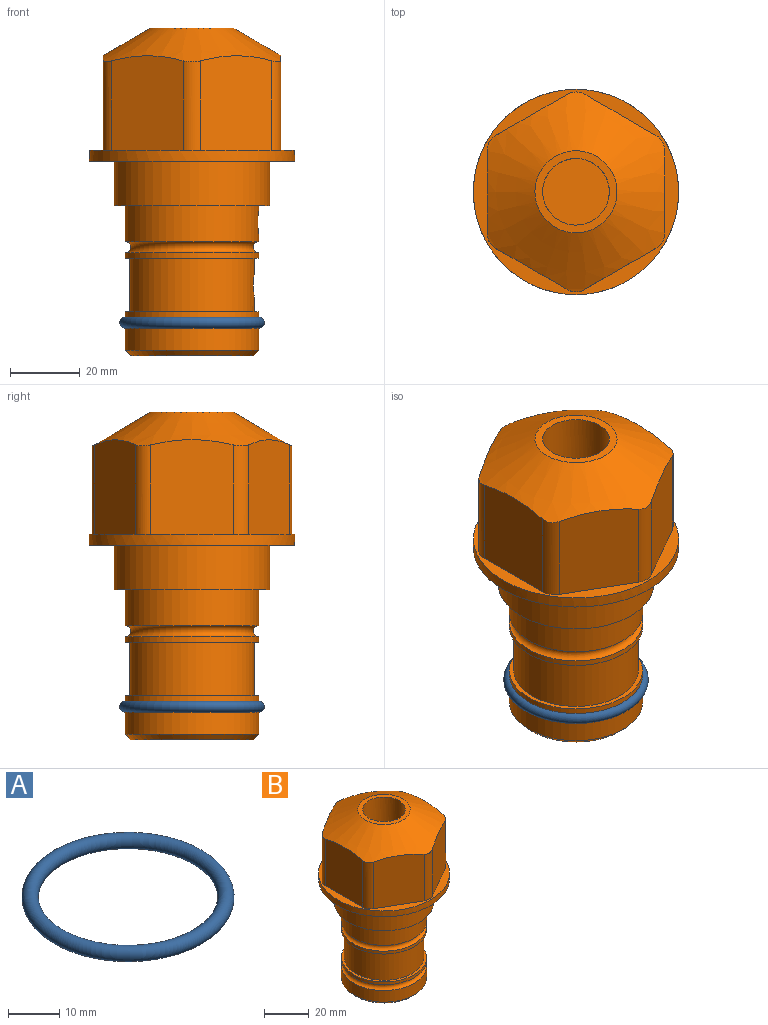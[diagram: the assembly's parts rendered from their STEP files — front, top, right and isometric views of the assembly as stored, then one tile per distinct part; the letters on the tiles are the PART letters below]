
ASSEMBLY  parts=2 mates=1
PART A: 1 faces, bbox 44.7x44.7x3.2 mm
  f0: torus R=19.05mm, axis (0,0,1), area 1193.9mm2
PART B: 36 faces, bbox 58.7x58.7x93.7 mm
  f0: cylinder r=17.78mm len=35.56mm, axis (0,0,1), area 1670.8mm2, adj f23,f24,f31
  f1: cylinder r=19.05mm len=38.1mm, axis (0,0,1), area 1191.9mm2, adj f26,f27,f30
  f2: plane 58.66x58.66mm, normal (0,0,-1), area 1150.6mm2, adj f3,f28
  f3: cylinder r=29.33mm len=58.66mm, axis (0,0,-1), area 585.1mm2, adj f2,f4
  f4: plane 58.66x58.66mm, normal (0,0,1), area 475.9mm2, adj f3,f5,f6,f7,f8,f9,f10,f11
  f5: plane 27.04x20.32mm, normal (-0.5,0.87,0), area 622.4mm2, adj f4,f15,f16,f17
  f6: plane 27.04x20.32mm, normal (0.5,0.87,0), area 622.4mm2, adj f4,f14,f15,f17
  f7: plane 27.04x23.48mm, normal (1,0,0), area 622.4mm2, adj f4,f13,f14,f17
  f8: plane 27.04x20.32mm, normal (0.5,-0.87,0), area 622.4mm2, adj f4,f12,f13,f17
  f9: plane 27.04x20.32mm, normal (-0.5,-0.87,0), area 622.4mm2, adj f4,f11,f12,f17
  f10: plane 27.04x23.48mm, normal (-1,0,0), area 622.4mm2, adj f4,f11,f16,f17
  f11: cylinder r=5.08mm len=25.55mm, axis (0,0,-1), area 134.7mm2, adj f4,f9,f10,f17
  f12: cylinder r=5.08mm len=25.55mm, axis (0,0,-1), area 134.7mm2, adj f4,f8,f9,f17
  f13: cylinder r=5.08mm len=25.55mm, axis (0,0,-1), area 134.7mm2, adj f4,f7,f8,f17
  f14: cylinder r=5.08mm len=25.55mm, axis (0,0,-1), area 134.7mm2, adj f4,f6,f7,f17
  f15: cylinder r=5.08mm len=25.55mm, axis (0,0,-1), area 134.7mm2, adj f4,f5,f6,f17
  f16: cylinder r=5.08mm len=25.55mm, axis (0,0,-1), area 134.7mm2, adj f4,f5,f10,f17
  f17: cone r=11.73mm half-angle=60deg, axis (0,0,-1), area 2071.8mm2, adj f5,f6,f7,f8,f9,f10,f11,f12
  f18: plane 23.46x23.46mm, normal (0,0,1), area 147.4mm2, adj f17,f35
  f19: plane 34.93x34.93mm, normal (0,0,-1), area 958mm2, adj f29
  f20: cylinder r=19.05mm len=38.1mm, axis (0,0,1), area 760.1mm2, adj f21,f29
  f21: torus R=19.05mm, axis (0,0,1), area 565.3mm2, adj f20,f22
  f22: cylinder r=19.05mm len=38.1mm, axis (0,0,1), area 190mm2, adj f21,f23
  f23: plane 38.1x38.1mm, normal (0,0,1), area 146.9mm2, adj f0,f22
  f24: plane 38.1x38.1mm, normal (0,0,-1), area 146.9mm2, adj f0,f25
  f25: cylinder r=19.05mm len=38.1mm, axis (0,0,1), area 190mm2, adj f24,f26
  f26: torus R=19.05mm, axis (0,0,1), area 565.3mm2, adj f1,f25
  f27: plane 44.45x44.45mm, normal (0,0,-1), area 411.7mm2, adj f1,f28
  f28: cylinder r=22.23mm len=44.45mm, axis (0,0,1), area 1773.5mm2, adj f2,f27
  f29: cone r=19.05mm half-angle=45deg, axis (0,0,1), area 257.5mm2, adj f19,f20
  f30: cylinder r=3.17mm len=6.75mm, axis (-1,0,0), area 128mm2, adj f1,f33
  f31: cylinder r=3.17mm len=6.35mm, axis (-1,0,0), area 102.5mm2, adj f0,f33
  f32: plane 25.4x25.4mm, normal (0,0,1), area 506.7mm2, adj f33
  f33: cylinder r=12.7mm len=66.42mm, axis (0,0,-1), area 5236.2mm2, adj f30,f31,f32,f34
  f34: cone r=9.53mm half-angle=30deg, axis (0,0,-1), area 443.4mm2, adj f33,f35
  f35: cylinder r=9.53mm len=19.05mm, axis (0,0,-1), area 1001mm2, adj f18,f34
PLACE A t=(0,0,-21.59)mm
PLACE B at identity fixed
MATE fastened A.f0 <-> B.f0  axis (0,0,1) through (0,0,-46.1)mm
